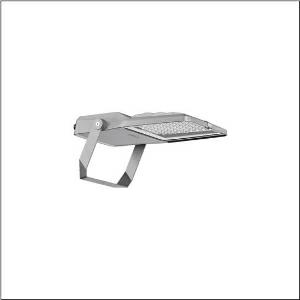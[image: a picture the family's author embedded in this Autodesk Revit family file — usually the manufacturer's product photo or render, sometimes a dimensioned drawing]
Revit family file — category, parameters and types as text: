
# Revit family: floodlight_fl_21_iq_mini___pl64_5xa7771d2e1a_0f9a
name_source: partatom
category: Lighting Fixtures
units: mm (PartAtom-declared; Revit-internal decimal feet)

## family parameters
Cut with Voids When Loaded = No
Host = Face
Light Source = No
Part Type = Normal
Room Calculation Point = No
Round Connector Dimension = Use Diameter
Shared = No

## types (1)
- --- (1 x LED, 17220 lm, 143 W, 3000K)
    Apparent Load = 143 VA
    CIE Flux Codes = 28 80 98 100 100
    Color Rendering = 70
    Color Temperature = 3000K
    Default Elevation = 1800 mm
    Description = Floodlight FL 21 iQ mini, floodlight, primary light control with lens, of PMMA, primary optical cover: protective disc, of toughened safety glass, transparent, light distribution: PL64, light emission: direct distribution, installation type: surface-mounted, lamps: LED, High Power LED, rated values: 17.220lm | 143W | 120,4lm/W (begin service life); end service life: 17.220lm | 151,6W; at 50% lumin. flux: 8.610lm | 60,6W | 142,1lm/W, colour temperature: 3000K, colour rendering: CRI > 70, light colour: 730, light setting 1 begin service life: 100% | 17.220lm | 143W | 120,4lm/W | 3.000K, light setting 1 end service life: 151,6W, further light settings possible, control: Auto-Match, Temp-Guard, Lumen-Switch, Night-Set, Smart-Wire, Light-Fading, Desk-Remote (wireless, voltage-free reading and setting of iQ features in the workshop via application-optimized NFC function/RFID function), optimised constant luminous flux control (CLO 2.0), pre-setting: linear dimming characteristic, with terminal, 6-pole, mains connection: 220..240V, AC, 50/60Hz, luminaire housing, of diecast aluminium, powder-coated, SITECO metallic grey (DB 702S), corrosivity category C5 mid according to DIN EN ISO 12944suitable for swimming poolschlorine-resistant, sealing non-destructively replaceable, mounting bracket, of steel, galvanised, powder-coated, SITECO metallic grey (DB 702S), protection rating (complete): IP66, insulation class (complete): insulation class II (safety insulation), certification: CE, ENEC, VDE, protection symbol: D, impact resistance: IK08, permissible operating ambient temperature: -40..+40°C, permissible operating ambient temperature for outdoor applications: -40..+50°C, standard: DIN EN 12944, LABS conformity tested according to VDMA 24364:2018-05, packaging unit: 1 piece

Light Distribution: PL64
    Height = 70 mm
    Lamp = 1 x LED
    Lamp Light Flux = 17220 lm
    Lamp Power = 143 W
    Lamp count = 1
    Length = 485 mm
    Luminous efficacy = 120 lm/W
    Manufacturer = Siteco
    ModVariant = No
    Model = 5XA7771D2E1A
    Number of Poles = 1
    OnlyDefault = Yes
    Power Factor = 1
    Product Name = Floodlight FL 21 iQ mini | PL64
    Product group = floodlight | pylon annexe
    ProductGroupID = 6201
    Protection Class = Protection class II
    Protection Degree = IP 66
    RLX_Detail_Level = 1
    RLX_Emergency_Light_Flux = 0 lm
    RLX_Emergency_Type = 0
    RLX_Emergency_Type_DB = No
    RlxData = <blob elided: 96825 chars, md5=a93d5cae>
    Socket = socket
    Standby Power = 0 W
    System Light Flux = 17220 lm
    System Power = 143 W
    Type Comments = factory setting: luminous flux: 100 % | dim-lin: 254 | 730 mA
    Type Image = l_1006845.jpg
    URL = http://relux.com
    VarID = @adj_165621
    Voltage = 0 V
    Weight = 0.00 kg
    Width = 337 mm

## geometry (parser evidence)
native form markers: Blend x4, Sweep x13
no freeform markers — native parametric forms only
